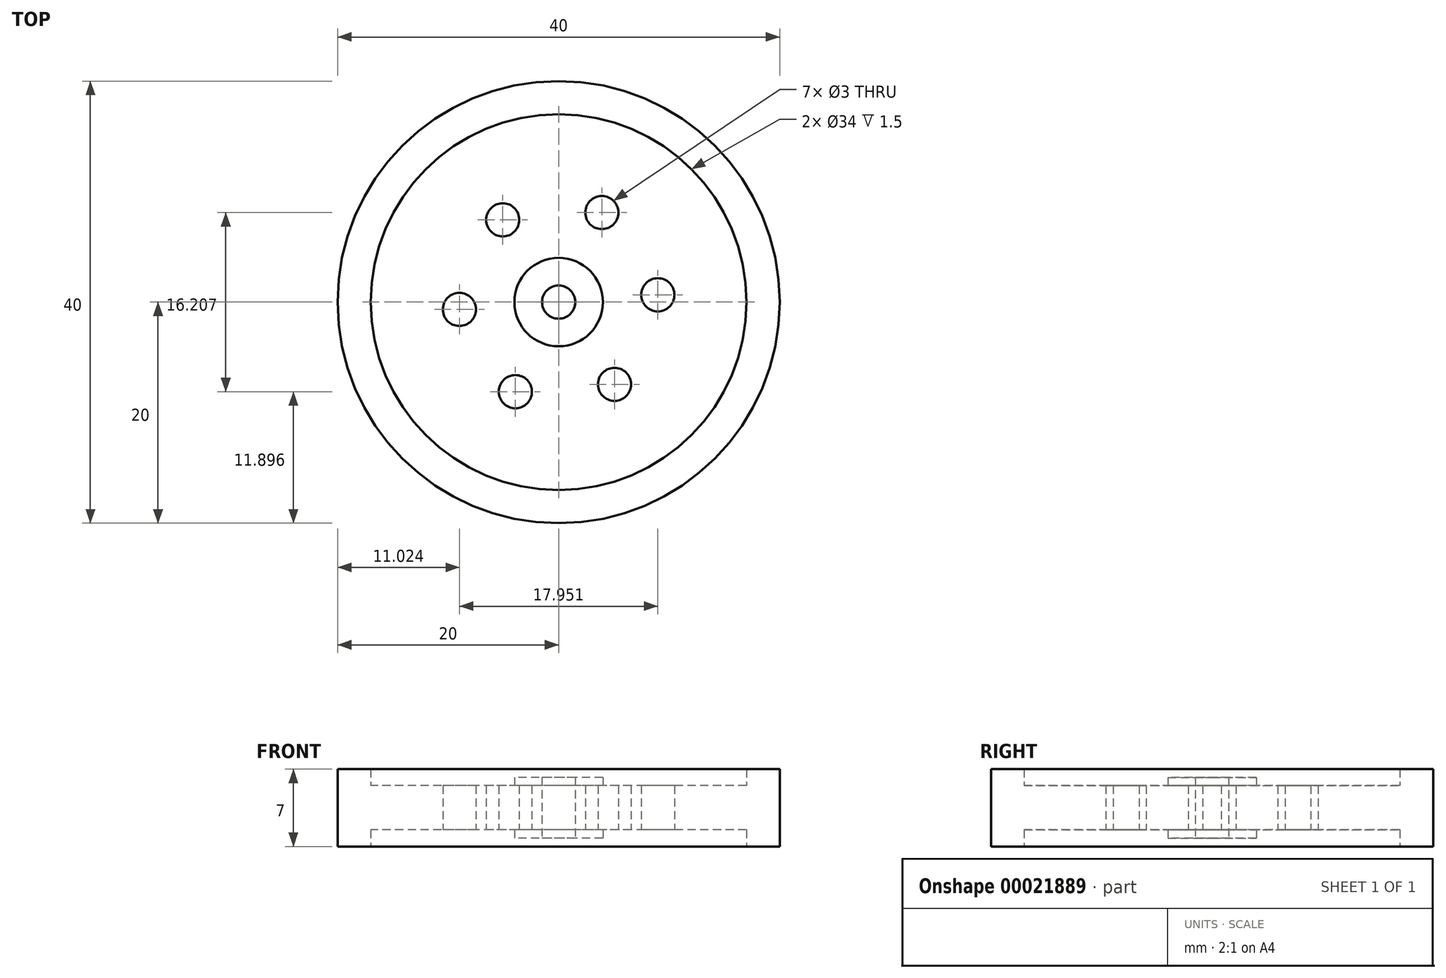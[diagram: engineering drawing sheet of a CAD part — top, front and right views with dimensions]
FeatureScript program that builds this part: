
annotation { "Feature Type Name" : "Feature", "Feature Type Description" : "" }
export const myFeature = defineFeature(function(context is Context, id is Id, definition is map)
    precondition{}
    {
        {
            var Q0;
            Q0=qCreatedBy(makeId("Top.planeOp"),FACE);
            var sketch = newSketch(context, id + "F0", { "sketchPlane" : qUnion([Q0])});
            skCircle(sketch, "E0", {"center": v(0, 0) * mm, "radius": 20 * mm});
            skCircle(sketch, "E1.cCircle", {"center": v(0, 0) * mm, "radius": 7.8 * mm, "construction": true});
            skLineSegment(sketch, "E1.0", {"start": v(-8.98, -0.66) * mm, "end": v(-5.06, 7.44) * mm});
            skLineSegment(sketch, "E1.1", {"start": v(-5.06, 7.44) * mm, "end": v(3.92, 8.1) * mm});
            skLineSegment(sketch, "E1.2", {"start": v(3.92, 8.1) * mm, "end": v(8.98, 0.66) * mm});
            skLineSegment(sketch, "E1.3", {"start": v(8.98, 0.66) * mm, "end": v(5.06, -7.44) * mm});
            skLineSegment(sketch, "E1.4", {"start": v(5.06, -7.44) * mm, "end": v(-3.92, -8.1) * mm});
            skLineSegment(sketch, "E1.5", {"start": v(-3.92, -8.1) * mm, "end": v(-8.98, -0.66) * mm});
            skPoint(sketch, "E1.0.midPoint", {"position": v(-7.02, 3.4) * mm});
            skCircle(sketch, "E2", {"center": v(-8.98, -0.66) * mm, "radius": 1.5 * mm});
            skCircle(sketch, "E3", {"center": v(-3.92, -8.1) * mm, "radius": 1.5 * mm});
            skCircle(sketch, "E4", {"center": v(5.06, -7.44) * mm, "radius": 1.5 * mm});
            skCircle(sketch, "E5", {"center": v(8.98, 0.66) * mm, "radius": 1.5 * mm});
            skCircle(sketch, "E6", {"center": v(3.92, 8.1) * mm, "radius": 1.5 * mm});
            skCircle(sketch, "E7", {"center": v(-5.06, 7.44) * mm, "radius": 1.5 * mm});
            skCircle(sketch, "E8", {"center": v(0, 0) * mm, "radius": 4 * mm});
            skCircle(sketch, "E9", {"center": v(0, 0) * mm, "radius": 1.5 * mm});
            skCircle(sketch, "E10", {"center": v(0, 0) * mm, "radius": 17 * mm});
            skSolve(sketch);
        }
        {
            var Q0;
            Q0=makeQuery(id+"F0.imprint","IMPRINT",FACE,{"disambiguationData":[TD([[makeQuery(id+"F0.imprint","IMPRINT",EDGE,{"derivedFrom":sQuery(id+"F0.wireOp",EDGE,"E0")}),1.0]])]});
            extrude(context, id + "F1", {"entities" : qUnion([Q0]), "endBound" : BoundingType.SYMMETRIC, "depth" : 7 * mm});
        }
        {
            var Q0;
            Q0=makeQuery(id+"F0.imprint","IMPRINT",FACE,{"disambiguationData":[TD([[makeQuery(id+"F0.imprint","IMPRINT",EDGE,{"derivedFrom":sQuery(id+"F0.wireOp",EDGE,"E10")}),1.0]])]});
            extrude(context, id + "F2", {"entities" : qUnion([Q0]), "operationType" : NewBodyOperationType.ADD, "endBound" : BoundingType.SYMMETRIC, "depth" : 4 * mm});
        }
        {
            var Q0;
            Q0=makeQuery(id+"F0.imprint","IMPRINT",FACE,{"disambiguationData":[TD([[makeQuery(id+"F0.imprint","IMPRINT",EDGE,{"derivedFrom":sQuery(id+"F0.wireOp",EDGE,"E8")}),-1.0]])]});
            extrude(context, id + "F3", {"entities" : qUnion([Q0]), "operationType" : NewBodyOperationType.ADD, "endBound" : BoundingType.SYMMETRIC, "depth" : 4 * mm});
        }
        {
            var Q0;
            Q0=makeQuery(id+"F0.imprint","IMPRINT",FACE,{"disambiguationData":[TD([[makeQuery(id+"F0.imprint","IMPRINT",EDGE,{"derivedFrom":sQuery(id+"F0.wireOp",EDGE,"E8")}),1.0]])]});
            extrude(context, id + "F4", {"entities" : qUnion([Q0]), "operationType" : NewBodyOperationType.ADD, "endBound" : BoundingType.SYMMETRIC, "depth" : 5.5 * mm});
        }
    });
